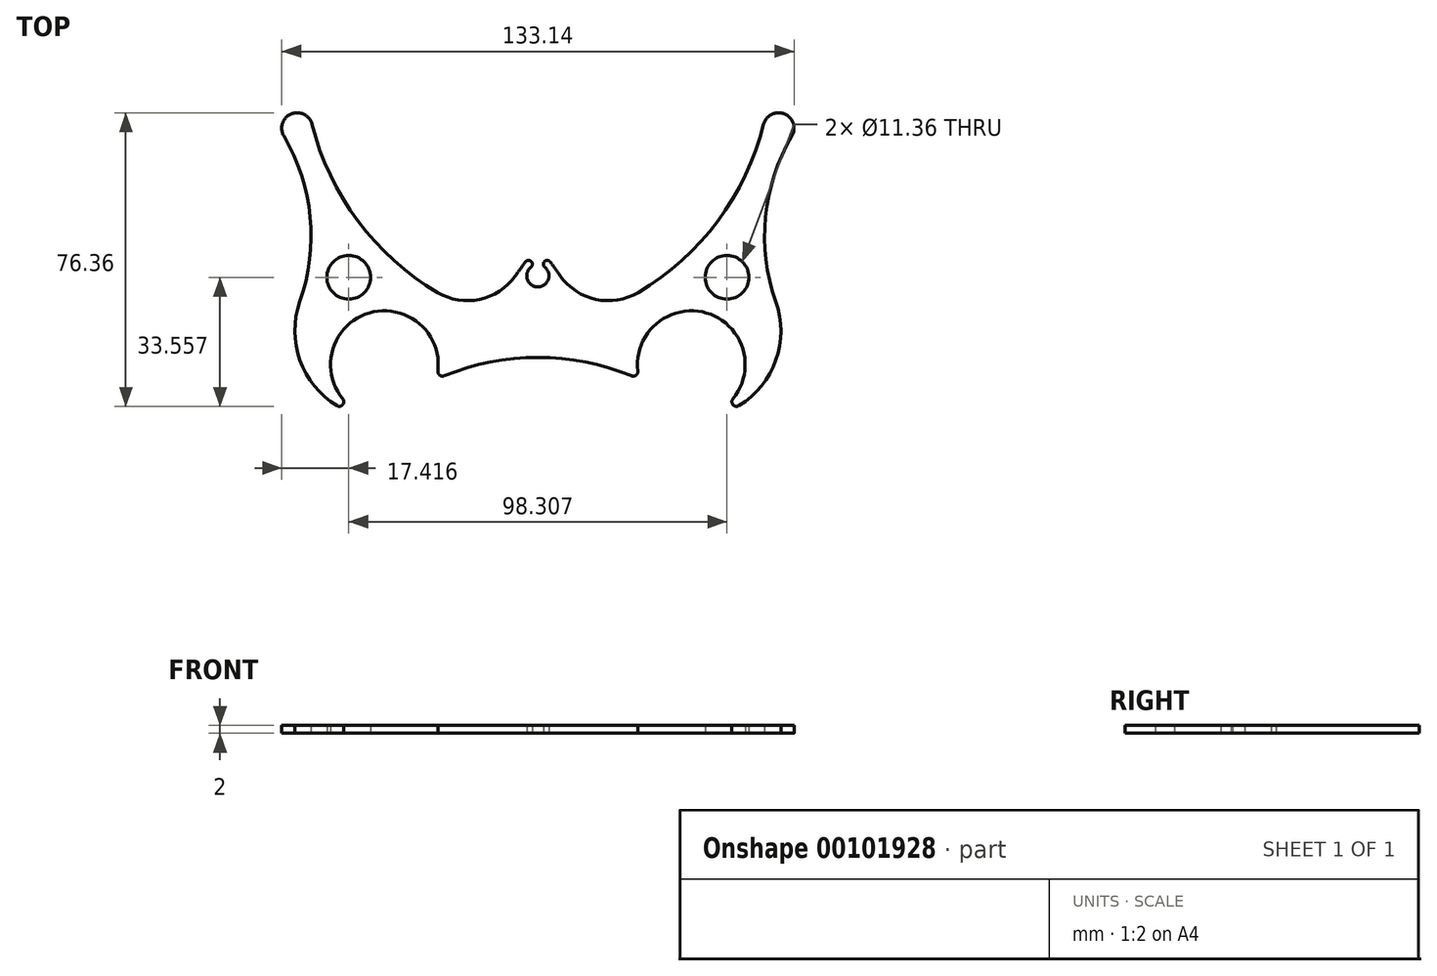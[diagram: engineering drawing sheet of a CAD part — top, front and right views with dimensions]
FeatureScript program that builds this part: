
annotation { "Feature Type Name" : "Feature", "Feature Type Description" : "" }
export const myFeature = defineFeature(function(context is Context, id is Id, definition is map)
    precondition{}
    {
        {
            var Q0;
            Q0=qCreatedBy(makeId("Top.planeOp"),FACE);
            var sketch = newSketch(context, id + "F0", { "sketchPlane" : qUnion([Q0])});
            skPoint(sketch, "E0.middle", {"position": v(0, 0) * mm});
            skArc(sketch, "E1", {"start": v(-25.98, -20.61) * mm, "mid": v(-43.8, -5.51) * mm, "end": v(-50.7, -27.83) * mm});
            skArc(sketch, "E2", {"start": v(-61.86, -2.56) * mm, "mid": v(-59.16, 19.45) * mm, "end": v(-66.02, 40.53) * mm});
            skArc(sketch, "E3", {"start": v(-58.7, 43.53) * mm, "mid": v(-46.77, 18.42) * mm, "end": v(-26.1, -0.18) * mm});
            skLineSegment(sketch, "E4", {"start": v(0, 29) * mm, "end": v(0, -29.02) * mm, "construction": true});
            skArc(sketch, "E5", {"start": v(-66.02, 40.53) * mm, "mid": v(-64.1, 46.26) * mm, "end": v(-58.7, 43.53) * mm});
            skArc(sketch, "E6", {"start": v(-61.86, -2.56) * mm, "mid": v(-61.85, -17.79) * mm, "end": v(-52.25, -29.62) * mm});
            skArc(sketch, "E7", {"start": v(-52.25, -29.62) * mm, "mid": v(-50.72, -29.38) * mm, "end": v(-50.7, -27.83) * mm});
            skArc(sketch, "E8", {"start": v(0, -17.06) * mm, "mid": v(-12.4, -18.28) * mm, "end": v(-24.33, -21.87) * mm});
            skArc(sketch, "E9", {"start": v(-24.33, -21.87) * mm, "mid": v(-25.51, -21.71) * mm, "end": v(-25.98, -20.61) * mm});
            skArc(sketch, "E10", {"start": v(-26.1, -0.18) * mm, "mid": v(-15.12, -1.98) * mm, "end": v(-5.83, 4.15) * mm});
            skArc(sketch, "E11", {"start": v(-5.83, 4.15) * mm, "mid": v(-4.54, 5.96) * mm, "end": v(-3.25, 7.76) * mm});
            skArc(sketch, "E12", {"start": v(-3.25, 7.76) * mm, "mid": v(-1.75, 7.9) * mm, "end": v(-1.8, 6.4) * mm});
            skArc(sketch, "E13", {"start": v(-1.8, 6.4) * mm, "mid": v(-2.72, 3.18) * mm, "end": v(0, 1.25) * mm});
            skCircle(sketch, "E14", {"center": v(-49.15, 3.76) * mm, "radius": 5.68 * mm});
            skArc(sketch, "E15.MirrorCS", {"start": v(52.25, -29.62) * mm, "mid": v(50.72, -29.38) * mm, "end": v(50.7, -27.83) * mm});
            skArc(sketch, "E16.MirrorCS", {"start": v(3.25, 7.76) * mm, "mid": v(1.75, 7.9) * mm, "end": v(1.8, 6.4) * mm});
            skArc(sketch, "E17.MirrorCS", {"start": v(5.83, 4.15) * mm, "mid": v(4.54, 5.96) * mm, "end": v(3.25, 7.76) * mm});
            skArc(sketch, "E18.MirrorCS", {"start": v(24.33, -21.87) * mm, "mid": v(25.51, -21.71) * mm, "end": v(25.98, -20.61) * mm});
            skArc(sketch, "E19.MirrorCS", {"start": v(1.8, 6.4) * mm, "mid": v(2.72, 3.18) * mm, "end": v(0, 1.25) * mm});
            skArc(sketch, "E20.MirrorCS", {"start": v(58.7, 43.53) * mm, "mid": v(46.77, 18.42) * mm, "end": v(26.1, -0.18) * mm});
            skArc(sketch, "E21.MirrorCS", {"start": v(26.1, -0.18) * mm, "mid": v(15.12, -1.98) * mm, "end": v(5.83, 4.15) * mm});
            skArc(sketch, "E22.MirrorCS", {"start": v(61.86, -2.56) * mm, "mid": v(61.85, -17.79) * mm, "end": v(52.25, -29.62) * mm});
            skArc(sketch, "E23.MirrorCS", {"start": v(61.86, -2.56) * mm, "mid": v(59.16, 19.45) * mm, "end": v(66.02, 40.53) * mm});
            skArc(sketch, "E24.MirrorCS", {"start": v(66.02, 40.53) * mm, "mid": v(64.1, 46.26) * mm, "end": v(58.7, 43.53) * mm});
            skArc(sketch, "E25.MirrorCS", {"start": v(0, -17.06) * mm, "mid": v(12.4, -18.28) * mm, "end": v(24.33, -21.87) * mm});
            skCircle(sketch, "E26.MirrorC", {"center": v(49.15, 3.76) * mm, "radius": 5.68 * mm});
            skArc(sketch, "E27.MirrorCS", {"start": v(25.98, -20.61) * mm, "mid": v(43.8, -5.51) * mm, "end": v(50.7, -27.83) * mm});
            skSolve(sketch);
        }
        {
            var Q0;
            Q0 = qSketchRegion(id + "F0", true);
            extrude(context, id + "F1", {"entities" : qUnion([Q0]), "depth" : 2 * mm});
        }
    });
